# Revit family: Plymold-Essentials-Jupiter-8_Seat_Rectangular-Quest
name_source: partatom
category: Furniture
units: mm (PartAtom-declared; Revit-internal decimal feet)

## family parameters
Always vertical = Yes
Cut with Voids When Loaded = No
OmniClass Number = 23.40.20.00
OmniClass Title = General Furniture and Specialties
Room Calculation Point = No
Shared = No
Work Plane-Based = No

## types (4) — shared parameters
Assembly Code = E2020200
Back Finish = PLY - Onyx Black Powdercoat
Base Finish = PLY - Onyx Black Powdercoat
Cap Finish = PLY - Plastic Black
Default Elevation = 0"
Depth = 53"
Edge Finish = PLY - Plastic Black
Frame Finish = PLY - Onyx Black Powdercoat
Glide Finish = PLY - Plastic Black
Hardware Finish = PLY - Onyx Black Powdercoat
Height = 29 3/4"
Keynote = 12500
Manufacturer = Plymold
Product Documentation Link = https://plymold.com
Revit File Built By = https://servex-us.com
Seat Finish = PLY - Plastic Blue
Support Finish = PLY - Onyx Black Powdercoat
Sustainability = https://plymold.com
Top Finish = PLY - Wood Mahogany
Type Comments = Quest
URL = https://plymold.com
Width = 96"

## per-type parameters (varying)
| type | DE | Description | PVC | TPD | VE |
| JURE008DEQU | Yes | 8 Seat Island Unit - Jupiter® Cluster w/Bullnose Dur-A-Edge® Table Top Unit - 96"W x 53"D x 29.75"H | No | No | No |
| JURE008TPDQU | No | 8 Seat Island Unit - Jupiter® Cluster w/Thin Dur-A-Edge® Table Top Unit - 96"W x 53"D x 29.75"H | No | Yes | No |
| JURE008VEQU | No | 8 Seat Island Unit - Jupiter® Cluster w/Vinyl Edge Table Top Unit - 96"W x 53"D x 29.75"H | No | No | Yes |
| JURE008PVCQU | No | 8 Seat Island Unit - Jupiter® Cluster w/PVC Edge Table Top Unit - 96"W x 53"D x 29.75"H | Yes | No | No |

note: column(s) folded — value = type name in every type: Model

## geometry (parser evidence)
native form markers: Sweep x9
no freeform markers — native parametric forms only
